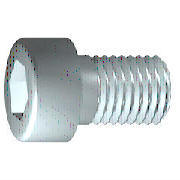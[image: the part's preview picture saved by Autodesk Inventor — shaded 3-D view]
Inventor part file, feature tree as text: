
AUTODESK INVENTOR PART (.ipt)
format: ipt  version: 2020 (Build 240168000, 168)  size: 189,952 bytes
history: native  units: mm (DEFAULTED — no unit token found)
features: sketch x2, other x1, extrude x1, plane x1, fillet x1
ambient origin geometry x7: Origin, YZ Plane, XY Plane, X Axis, Y Axis, Z Axis, Center Point
bodies: Solid1 (feature_tree)
feature tree (6):
  other  "Bryła"
  extrude  "Szczelina"  Depth=22.0mm
  plane  "Work Plane1"
  fillet  "Fillet2"  Radius=0.49086mm
  sketch  "Szkic1"
  sketch  "Szkic2"
